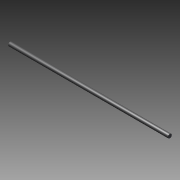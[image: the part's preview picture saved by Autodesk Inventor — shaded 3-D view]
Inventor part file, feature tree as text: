
AUTODESK INVENTOR PART (.ipt)
format: ipt  version: 2014 SP1 (Build 180222100, 222)  size: 83,968 bytes
history: native  units: mm
features: revolve x1, sketch x1
ambient origin geometry x8: Origin, YZ Plane, XZ Plane, XY Plane, X Axis, Y Axis, Z Axis, Center Point
bodies: Solid1 (feature_tree)
feature tree (2):
  revolve  "Revolution1"  [1 undecoded]
  sketch  "Sketch_3"  dims[d0=360.0deg d1=380.0mm]
note: 1 required parameter value undecoded (feature->parameter linkage not recoverable at this tier; creation-order binding heuristic only, values carry confidence <= 0.55)
